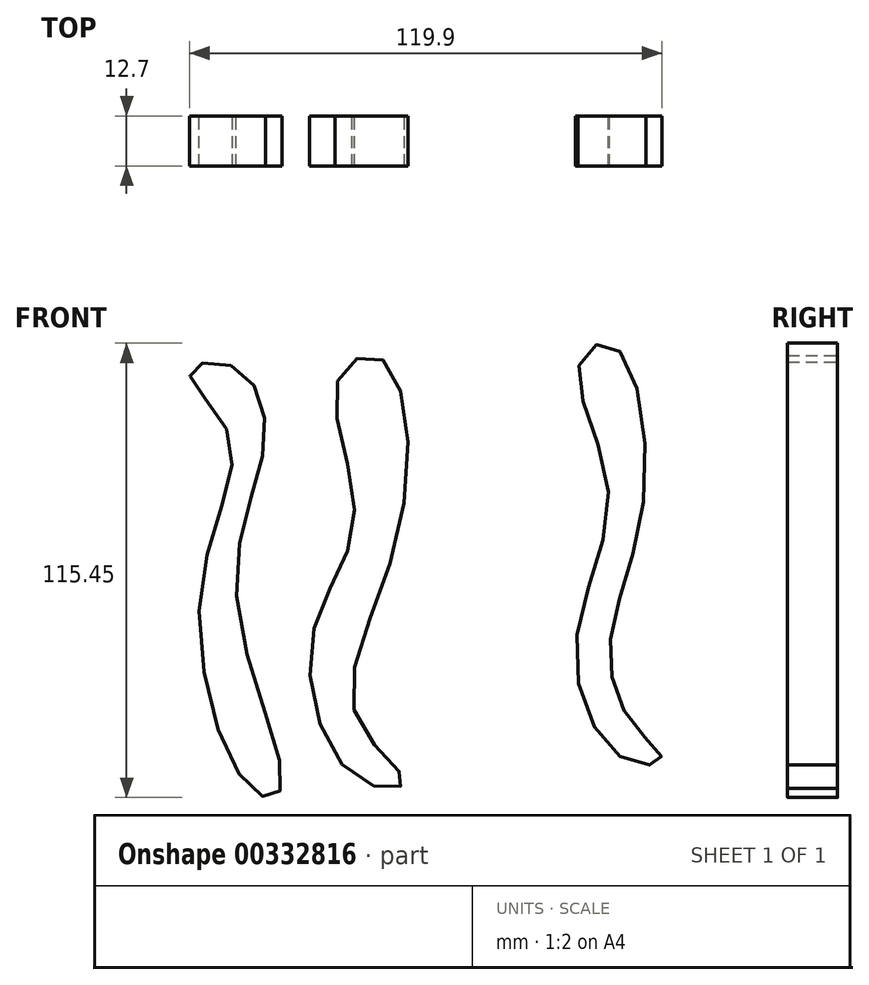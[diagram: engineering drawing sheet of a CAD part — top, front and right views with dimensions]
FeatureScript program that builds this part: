
annotation { "Feature Type Name" : "Feature", "Feature Type Description" : "" }
export const myFeature = defineFeature(function(context is Context, id is Id, definition is map)
    precondition{}
    {
        {
            var Q0;
            Q0=qCreatedBy(makeId("Front.planeOp"),FACE);
            var sketch = newSketch(context, id + "F0", { "sketchPlane" : qUnion([Q0])});
            skFitSpline(sketch, "E0", {"points": [v(-24.83, 58.16) * mm, v(-20.47, 23.3) * mm, v(-31.37, -7.62) * mm, v(-19.6, -42.91) * mm, v(-7.84, -43.78) * mm, v(-20.04, -27.23) * mm, v(-9.15, 20.26) * mm, v(-13.94, 63.82) * mm, v(-24.83, 58.16) * mm]});
            skFitSpline(sketch, "E1", {"points": [v(3.49, 64.26) * mm, v(11.33, 25.48) * mm, v(3.49, -10.67) * mm, v(17.43, -42.04) * mm, v(26.14, -41.17) * mm, v(18.73, -31.58) * mm, v(12.63, -10.67) * mm, v(20.91, 25.92) * mm, v(12.63, 67.3) * mm, v(3.49, 64.26) * mm]});
            skFitSpline(sketch, "E2", {"points": [v(36.6, 62.08) * mm, v(44, 30.28) * mm, v(35.72, -10.24) * mm, v(48.36, -38.12) * mm, v(57.5, -38.12) * mm, v(50.53, -29.4) * mm, v(44.43, -8.5) * mm, v(53.15, 29.4) * mm, v(44.87, 67.3) * mm, v(36.6, 62.08) * mm]});
            skSolve(sketch);
        }
        {
            var Q0;
            Q0=makeQuery(id+"F0.imprint","IMPRINT",FACE,{"disambiguationData":[TD([[makeQuery(id+"F0.imprint","IMPRINT",EDGE,{"derivedFrom":sQuery(id+"F0.wireOp",EDGE,"E0")}),1.0]])]});
            var Q1;
            Q1=makeQuery(id+"F0.imprint","IMPRINT",FACE,{"disambiguationData":[TD([[makeQuery(id+"F0.imprint","IMPRINT",EDGE,{"derivedFrom":sQuery(id+"F0.wireOp",EDGE,"E2")}),1.0]])]});
            extrude(context, id + "F1", {"entities" : qUnion([Q0, Q1]), "depth" : 12.7 * mm});
        }
        {
            var Q0;
            Q0=qCreatedBy(makeId("Front.planeOp"),FACE);
            var sketch = newSketch(context, id + "F2", { "sketchPlane" : qUnion([Q0])});
            skFitSpline(sketch, "E3", {"points": [v(-51.84, 62.08) * mm, v(-43.13, 44.65) * mm, v(-50.53, 3.7) * mm, v(-39.2, -45.52) * mm, v(-45.74, -46.4) * mm, v(-59.68, 4.14) * mm, v(-52.28, 44.22) * mm, v(-62.3, 60.34) * mm, v(-51.84, 62.08) * mm]});
            skSolve(sketch);
        }
        {
            var Q0;
            Q0=makeQuery(id+"F2.imprint","IMPRINT",FACE,{"disambiguationData":[TD([[makeQuery(id+"F2.imprint","IMPRINT",EDGE,{"derivedFrom":sQuery(id+"F2.wireOp",EDGE,"E3")}),-1.0]])]});
            extrude(context, id + "F3", {"entities" : qUnion([Q0]), "depth" : 12.7 * mm});
        }
    });
